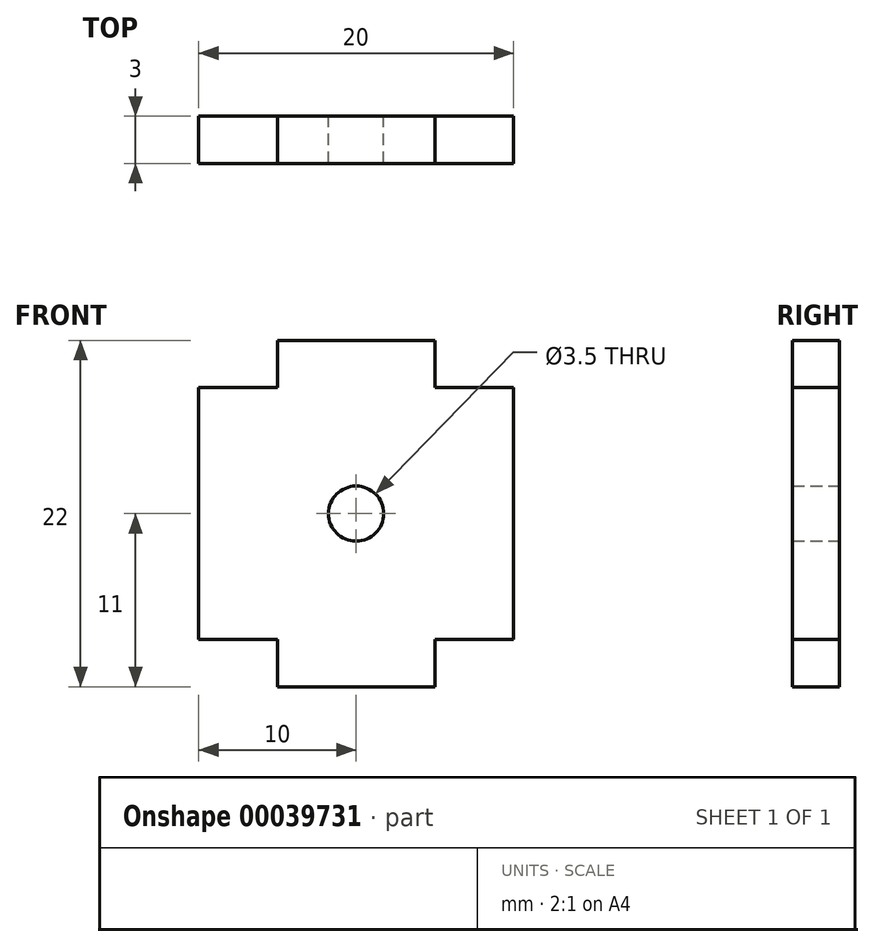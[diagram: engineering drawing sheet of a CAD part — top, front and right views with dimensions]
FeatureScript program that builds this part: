
annotation { "Feature Type Name" : "Feature", "Feature Type Description" : "" }
export const myFeature = defineFeature(function(context is Context, id is Id, definition is map)
    precondition{}
    {
        {
            var Q0;
            Q0=qCreatedBy(makeId("Front.planeOp"),FACE);
            var sketch = newSketch(context, id + "F0", { "sketchPlane" : qUnion([Q0])});
            skCircle(sketch, "E0", {"center": v(0, 0) * mm, "radius": 1.75 * mm});
            skLineSegment(sketch, "E1.rect.bottom", {"start": v(10, 8) * mm, "end": v(-10, 8) * mm});
            skLineSegment(sketch, "E1.rect.top", {"start": v(10, -8) * mm, "end": v(-10, -8) * mm});
            skLineSegment(sketch, "E1.rect.left", {"start": v(10, 8) * mm, "end": v(10, -8) * mm});
            skLineSegment(sketch, "E1.rect.right", {"start": v(-10, 8) * mm, "end": v(-10, -8) * mm});
            skLineSegment(sketch, "E2.bottom", {"start": v(-5, 8) * mm, "end": v(5, 8) * mm});
            skLineSegment(sketch, "E2.top", {"start": v(-5, 11) * mm, "end": v(5, 11) * mm});
            skLineSegment(sketch, "E2.left", {"start": v(-5, 8) * mm, "end": v(-5, 11) * mm});
            skLineSegment(sketch, "E2.right", {"start": v(5, 8) * mm, "end": v(5, 11) * mm});
            skPoint(sketch, "E3.oppositeSnap0", {"position": v(5, 9.5) * mm});
            skLineSegment(sketch, "E3.bottom", {"start": v(-5, -8) * mm, "end": v(5, -8) * mm});
            skLineSegment(sketch, "E3.top", {"start": v(-5, -11) * mm, "end": v(5, -11) * mm});
            skLineSegment(sketch, "E3.left", {"start": v(-5, -8) * mm, "end": v(-5, -11) * mm});
            skLineSegment(sketch, "E3.right", {"start": v(5, -8) * mm, "end": v(5, -11) * mm});
            skSolve(sketch);
        }
        {
            var Q0;
            Q0 = qSketchRegion(id + "F0", true);
            extrude(context, id + "F1", {"entities" : qUnion([Q0]), "depth" : 3 * mm});
        }
    });
